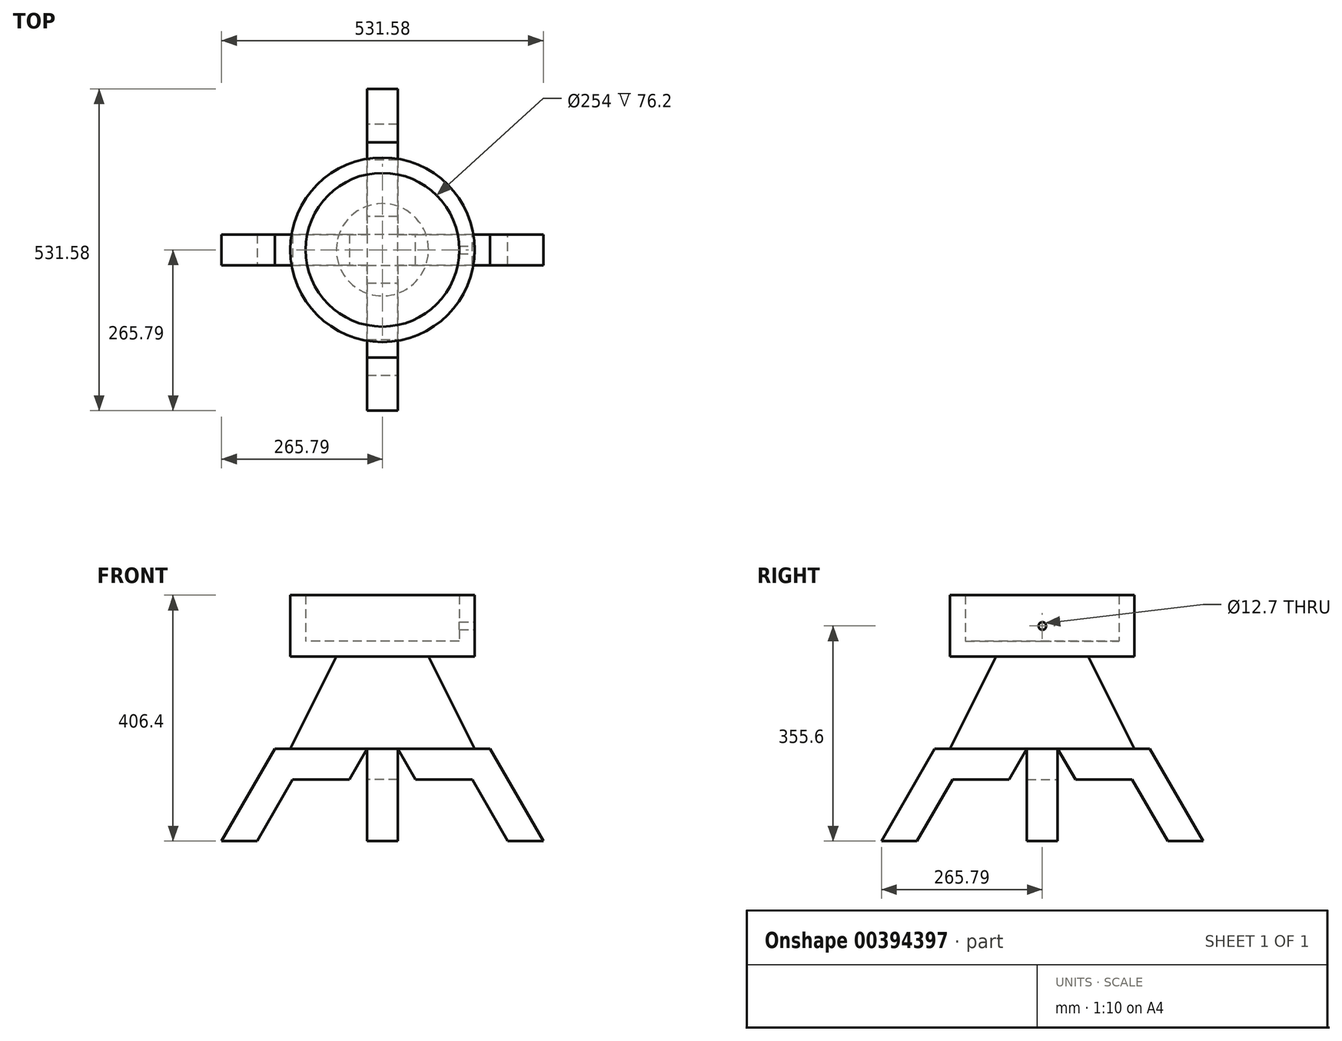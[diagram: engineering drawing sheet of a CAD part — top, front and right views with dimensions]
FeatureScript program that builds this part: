
annotation { "Feature Type Name" : "Feature", "Feature Type Description" : "" }
export const myFeature = defineFeature(function(context is Context, id is Id, definition is map)
    precondition{}
    {
        {
            var Q0;
            Q0=qCreatedBy(makeId("Top.planeOp"),FACE);
            var sketch = newSketch(context, id + "F0", { "sketchPlane" : qUnion([Q0])});
            skCircle(sketch, "E0", {"center": v(0, 0) * mm, "radius": 152.4 * mm});
            skSolve(sketch);
        }
        {
            var Q0;
            Q0=makeQuery(id+"F0.imprint","IMPRINT",FACE,{"disambiguationData":[TD([[makeQuery(id+"F0.imprint","IMPRINT",EDGE,{"derivedFrom":sQuery(id+"F0.wireOp",EDGE,"E0")}),1.0]])]});
            cPlane(context, id + "F1", {"entities" : qUnion([Q0]), "cplaneType" : CPlaneType.OFFSET, "offset" : 152.4 * mm, "width" : 152.4 * mm, "height" : 152.4 * mm});
        }
        {
            var Q0;
            Q0=qCreatedBy(id+"F1.planeOp",FACE);
            var sketch = newSketch(context, id + "F2", { "sketchPlane" : qUnion([Q0])});
            skCircle(sketch, "E1", {"center": v(0, 0) * mm, "radius": 76.2 * mm});
            skCircle(sketch, "E2", {"center": v(0, 0) * mm, "radius": 152.4 * mm});
            skCircle(sketch, "E3", {"center": v(0, 0) * mm, "radius": 127 * mm});
            skSolve(sketch);
        }
        {
            var Q0;
            Q0=makeQuery(id+"F0.imprint","IMPRINT",FACE,{"disambiguationData":[TD([[makeQuery(id+"F0.imprint","IMPRINT",EDGE,{"derivedFrom":sQuery(id+"F0.wireOp",EDGE,"E0")}),1.0]])]});
            var Q1;
            Q1=makeQuery(id+"F2.imprint","IMPRINT",FACE,{"disambiguationData":[TD([[makeQuery(id+"F2.imprint","IMPRINT",EDGE,{"derivedFrom":sQuery(id+"F2.wireOp",EDGE,"E1")}),1.0]])]});
            loft(context, id + "F3", {"sheetProfilesArray" : [{ "sheetProfileEntities" : qUnion([Q0]) }, { "sheetProfileEntities" : qUnion([Q1]) }]});
        }
        {
            var Q0;
            Q0=qCreatedBy(makeId("Front.planeOp"),FACE);
            var sketch = newSketch(context, id + "F4", { "sketchPlane" : qUnion([Q0])});
            skLineSegment(sketch, "E4", {"start": v(0, 0) * mm, "end": v(25.4, 0) * mm});
            skLineSegment(sketch, "E5", {"start": v(25.4, 0) * mm, "end": v(54.73, -50.8) * mm});
            skLineSegment(sketch, "E6", {"start": v(54.73, -50.8) * mm, "end": v(148.47, -50.8) * mm});
            skLineSegment(sketch, "E7", {"start": v(148.47, -50.8) * mm, "end": v(207.13, -152.4) * mm});
            skLineSegment(sketch, "E8", {"start": v(207.13, -152.4) * mm, "end": v(265.79, -152.4) * mm});
            skLineSegment(sketch, "E9", {"start": v(265.79, -152.4) * mm, "end": v(177.8, 0) * mm});
            skLineSegment(sketch, "E10", {"start": v(177.8, 0) * mm, "end": v(25.4, 0) * mm});
            skLineSegment(sketch, "E11", {"start": v(0, 0) * mm, "end": v(0, 76.2) * mm});
            skSolve(sketch);
        }
        {
            var Q0;
            Q0=makeQuery(id+"F4.imprint","IMPRINT",FACE,{"disambiguationData":[TD([[makeQuery(id+"F4.imprint","IMPRINT",EDGE,{"derivedFrom":sQuery(id+"F4.wireOp",EDGE,"E5")}),1.0]])]});
            extrude(context, id + "F5", {"entities" : qUnion([Q0]), "operationType" : NewBodyOperationType.ADD, "endBound" : BoundingType.SYMMETRIC, "depth" : 50.8 * mm});
        }
        {
            var Q0;
            Q0=makeQuery(id+"F3.opLoft","SWEPT_BODY",BODY,{"disambiguationData":[OSD([makeQuery(id+"F0.imprint","IMPRINT",FACE,{"disambiguationData":[TD([[makeQuery(id+"F0.imprint","IMPRINT",EDGE,{"derivedFrom":sQuery(id+"F0.wireOp",EDGE,"E0")}),1.0]])]}),makeQuery(id+"F2.imprint","IMPRINT",FACE,{"disambiguationData":[TD([[makeQuery(id+"F2.imprint","IMPRINT",EDGE,{"derivedFrom":sQuery(id+"F2.wireOp",EDGE,"E1")}),1.0]])]})])]});
            var Q1;
            Q1=sQuery(id+"F4.wireOp",EDGE,"E11");
            circularPattern(context, id + "F6", {"operationType" : NewBodyOperationType.ADD, "entities" : qUnion([Q0]), "axis" : qUnion([Q1]), "angle" : 360 * degree, "instanceCount" : 4, "equalSpace" : true});
        }
        {
            var Q0;
            Q0=makeQuery(id+"F2.imprint","IMPRINT",FACE,{"disambiguationData":[TD([[makeQuery(id+"F2.imprint","IMPRINT",EDGE,{"derivedFrom":sQuery(id+"F2.wireOp",EDGE,"E1")}),-1.0]])]});
            var Q1;
            Q1=makeQuery(id+"F2.imprint","IMPRINT",FACE,{"disambiguationData":[TD([[makeQuery(id+"F2.imprint","IMPRINT",EDGE,{"derivedFrom":sQuery(id+"F2.wireOp",EDGE,"E2")}),1.0]])]});
            var Q2;
            Q2=makeQuery(id+"F2.imprint","IMPRINT",FACE,{"disambiguationData":[TD([[makeQuery(id+"F2.imprint","IMPRINT",EDGE,{"derivedFrom":sQuery(id+"F2.wireOp",EDGE,"E1")}),1.0]])]});
            extrude(context, id + "F7", {"entities" : qUnion([Q0, Q1, Q2]), "operationType" : NewBodyOperationType.ADD, "depth" : 25.4 * mm});
        }
        {
            var Q0;
            Q0=makeQuery(id+"F2.imprint","IMPRINT",FACE,{"disambiguationData":[TD([[makeQuery(id+"F2.imprint","IMPRINT",EDGE,{"derivedFrom":sQuery(id+"F2.wireOp",EDGE,"E2")}),1.0]])]});
            extrude(context, id + "F8", {"entities" : qUnion([Q0]), "operationType" : NewBodyOperationType.ADD, "depth" : 101.6 * mm});
        }
        {
            var Q0;
            Q0=qCreatedBy(makeId("Right.planeOp"),FACE);
            cPlane(context, id + "F9", {"entities" : qUnion([Q0]), "cplaneType" : CPlaneType.OFFSET, "offset" : 152.4 * mm, "width" : 152.4 * mm, "height" : 152.4 * mm});
        }
        {
            var Q0;
            Q0=qCreatedBy(id+"F9.planeOp",FACE);
            var sketch = newSketch(context, id + "F10", { "sketchPlane" : qUnion([Q0])});
            skCircle(sketch, "E12", {"center": v(0, 203.2) * mm, "radius": 6.35 * mm});
            skSolve(sketch);
        }
        {
            var Q0;
            Q0=makeQuery(id+"F10.imprint","IMPRINT",FACE,{"disambiguationData":[TD([[makeQuery(id+"F10.imprint","IMPRINT",EDGE,{"derivedFrom":sQuery(id+"F10.wireOp",EDGE,"E12")}),1.0]])]});
            extrude(context, id + "F11", {"entities" : qUnion([Q0]), "operationType" : NewBodyOperationType.REMOVE, "oppositeDirection" : true, "depth" : 76.2 * mm});
        }
    });
